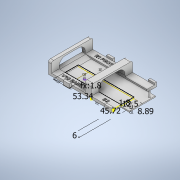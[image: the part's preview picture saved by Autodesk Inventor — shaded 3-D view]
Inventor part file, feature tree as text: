
AUTODESK INVENTOR PART (.ipt)
format: ipt  version: 2021 (Build 250183000, 183)  size: 1,575,936 bytes
history: native  units: in
note: dims shown in document units (in); Inventor stores cm internally (conversion verified against a paired STEP export)
features: sketch x12, extrude x11, mirror x3, plane x2, fillet x2, chamfer x1
ambient origin geometry x8: Origin, YZ Plane, XZ Plane, XY Plane, X Axis, Y Axis, Z Axis, Center Point
bodies: Solid1 (feature_tree)
feature tree (31):
  extrude  "Extrusion1"  Depth=0.7756in
  extrude  "Extrusion2"  Depth=0.0945in
  plane  "Work Plane1"
  extrude  "Extrusion3"  Depth=0.2362in
  sketch  "Sketch5"  dims[d14=1.3386in d15=0.0in]
  extrude  "Extrusion4"  TaperAngle=0.0deg  [1 undecoded]
  sketch  "Sketch7"  dims[d19=0.8268in d20=0.378in d21=0.0in d22=0.7756in]
  extrude  "Extrusion5"  Depth=0.2362in
  plane  "Work Plane2"
  mirror  "Mirror2"
  extrude  "Extrusion8"  Depth=0.378in
  fillet  "Fillet3"  [1 undecoded]
  fillet  "Fillet4"  Radius=0.7756in
  sketch  "Sketch13"  dims[d27=0.0in d29=-0.748in d30=0.748in]
  extrude  "Extrusion9"  Depth=0.378in
  mirror  "Mirror3"
  extrude  "Extrusion10"  Depth=1.4803in
  chamfer  "Chamfer1"  Distance=0.748in
  extrude  "Extrusion11"  Depth=0.4921in
  extrude  "Extrusion12"  Depth=0.0551in
  extrude  "Extrusion13"  Depth=0.0945in
  mirror  "Mirror4"
  sketch  "Sketch1"  dims[d5=2.4409in d6=0.7756in]
  sketch  "Sketch3"  dims[d7=0.0945in d8=0.0in d9=0.2362in]
  sketch  "Sketch4"  dims[d10=0.0787in d11=0.0in d13=0.2362in]
  sketch  "Sketch6"  dims[d16=0.063in d17=0.0in d18=0.2362in]
  sketch  "Sketch8"  dims[d23=0.378in d24=0.4921in]
  sketch  "Sketch12"  dims[d25=0.3189in d26=1.4803in]
  sketch  "Sketch14"  dims[d41=2.1in d42=0.4921in]
  sketch  "Sketch15"  dims[d43=0.0551in d44=0.0in d46=0.0787in]
  sketch  "Sketch16"  dims[d47=0.2756in d48=0.0709in d49=0.0709in d50=1.8in d51=0.35in d52=0.1575in d53=0.0in d54=0.1969in d55=0.0in d56=0.1969in d57=0.0551in d58=45.0deg d59=0.0787in d60=0.0787in d61=0.0394in d62=0.0394in d63=0.0394in d64=0.0394in d65=0.0787in d66=0.0787in d67=0.0394in d68=0.0in d69=0.0in d70=0.0in d71=0.2397in d72=0.2397in d73=0.9843in d74=0.315in d75=0.0in d76=0.2362in d77=0.0394in d78=0.0in d79=0.0945in]
note: 2 required parameter values undecoded (feature->parameter linkage not recoverable at this tier; creation-order binding heuristic only, values carry confidence <= 0.55)
